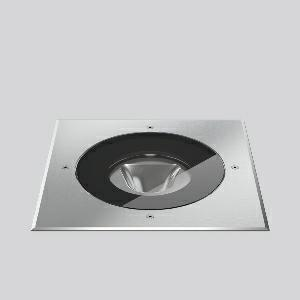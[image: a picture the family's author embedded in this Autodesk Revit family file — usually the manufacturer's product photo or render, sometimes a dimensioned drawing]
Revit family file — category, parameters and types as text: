
# Revit family: terra_edelstahl_245_641289_000_1_eaf0
name_source: partatom
category: Lighting Fixtures
units: mm (PartAtom-declared; Revit-internal decimal feet)

## family parameters
Cut with Voids When Loaded = No
Host = Face
Light Source = No
Part Type = Normal
Room Calculation Point = No
Round Connector Dimension = Use Diameter
Shared = No

## types (1)
- TERRA EDELSTAHL 245 (1 x LED Modul 840, 2200 lm, 4000)
    Apparent Load = 28 VA
    CIE Flux Codes = 0 0 0 0 100
    Color Rendering = 80
    Color Temperature = 4000
    Default Elevation = 1800 mm
    Description = Series: TERRA EDELSTAHL 245
In-ground luminaire for pedestrian areas. Housing made of corrosion-resistant die-cast aluminium, powder-coated. Marine grade stainless steel square shaped cover and screws. Flush mounted toughened glass. High-performance LED freeform mirror optics with asymmetrical light distribution. Integral flexible power cord H07-RN8F. Use of in-ground support is necessary, please order chosen version for your application separately. 
Colour: stainless steel
Length: 245 mm
Width: 245 mm
Height: 2 mm
Lamp: LED
System power: 28 W
Rated luminous flux: 2200 lm
Luminous efficiency: 79 lm/W
Control gear: Converter not necessary
Protection class: I
Type of protection: IP 68
    Height = 0 mm  [stored 0 ft]
    Lamp = 1 x LED Modul 840
    Lamp Light Flux = 2200 lm
    Lamp count = 1
    Length = 245 mm
    Lifetime = 50000 h
    Luminous efficacy = 79 lm/W
    Manufacturer = RZB
    ModVariant = No
    Model = 641289.000.1
    Mounting Place = Floor
    Mounting Type = Recessed
    Number of Poles = 1
    OnlyDefault = Yes
    Power Factor = 1
    Product Name = TERRA EDELSTAHL 245
    Product group = Ground recessed luminaire
    ProductGroupID = 3381
    Protection Class = Protection class I
    Protection Degree = IP 68
    RLX_Detail_Level = 1
    RLX_Emergency_Light_Flux = 0 lm
    RLX_Emergency_Type = 0
    RLX_Emergency_Type_DB = No
    RlxData = <blob elided: 52409 chars, md5=6754f48e>
    Socket = socket
    Standby Power = 0 W
    System Light Flux = 2200 lm
    System Power = 28 W
    Type Comments = ALEA SPOT
    Type Image = 641289.000.jpg
    URL = http://relux.com
    VarID = ---
    Voltage = 230 V
    Voltage Range = 220-240 V
    Weight = 0.00 kg
    Width = 245 mm

note: [stored X ft] marks values corroborated as IEEE doubles in the binary element streams (Revit-internal decimal feet)

## geometry (parser evidence)
native form markers: Blend x4, Sweep x9
no freeform markers — native parametric forms only
